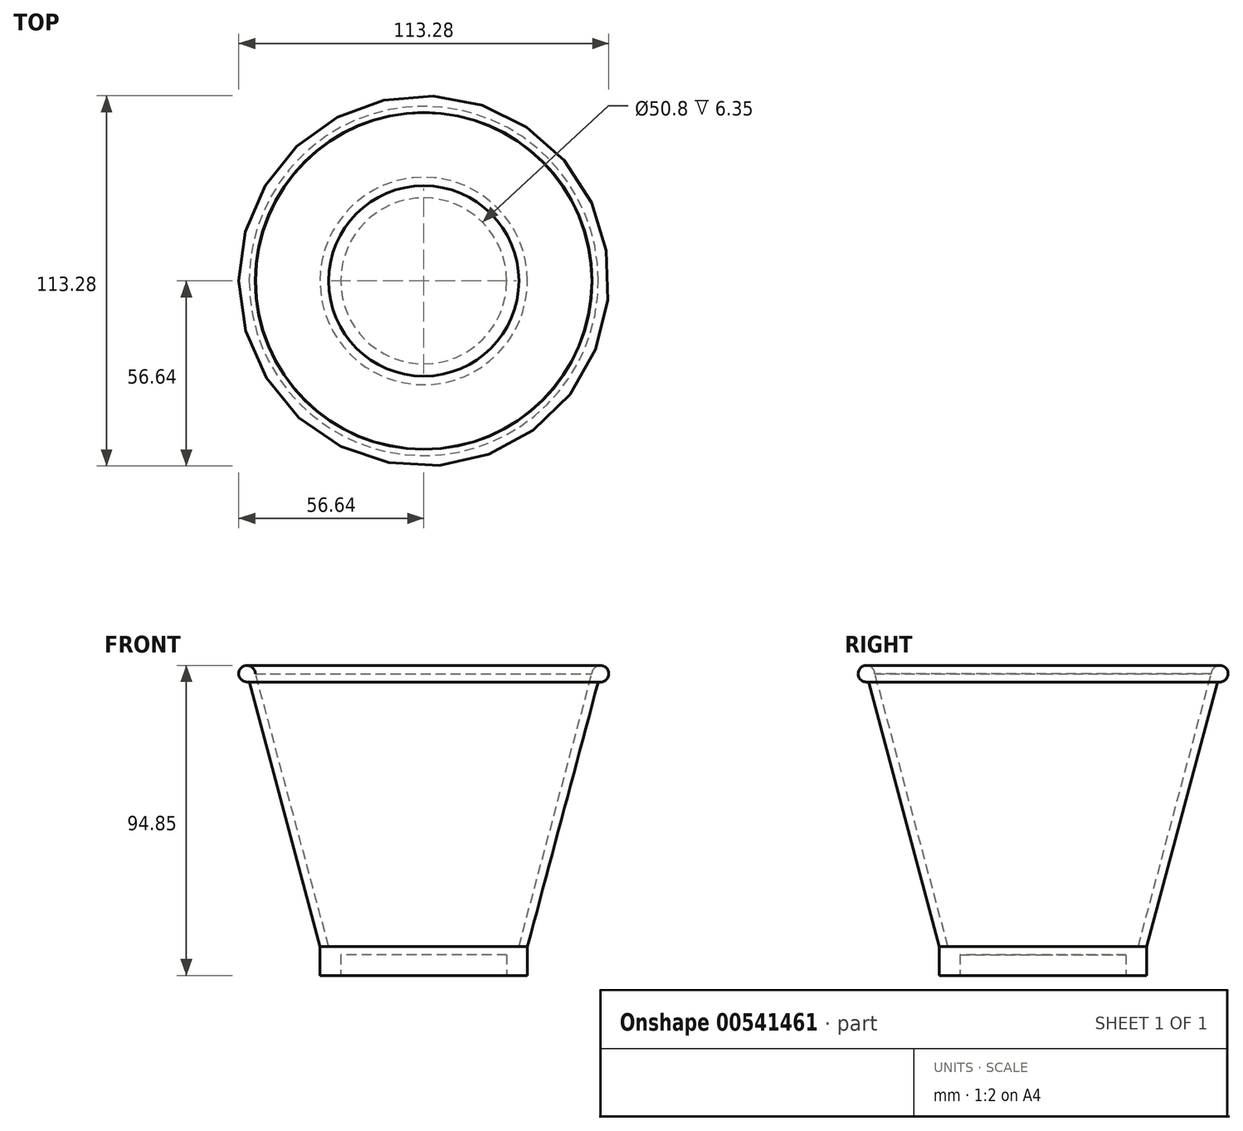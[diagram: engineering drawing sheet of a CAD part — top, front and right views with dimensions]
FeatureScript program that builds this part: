
annotation { "Feature Type Name" : "Feature", "Feature Type Description" : "" }
export const myFeature = defineFeature(function(context is Context, id is Id, definition is map)
    precondition{}
    {
        {
            var Q0;
            Q0=qCreatedBy(makeId("Top.planeOp"),FACE);
            var sketch = newSketch(context, id + "F0", { "sketchPlane" : qUnion([Q0])});
            skCircle(sketch, "E0", {"center": v(0, 0) * mm, "radius": 25.4 * mm});
            skCircle(sketch, "E1.0", {"center": v(0, 0) * mm, "radius": 31.75 * mm});
            skSolve(sketch);
        }
        {
            var Q0;
            Q0 = qSketchRegion(id + "F0", true);
            extrude(context, id + "F1", {"entities" : qUnion([Q0]), "depth" : 6.35 * mm, "offsetDistance" : 25.4 * mm});
        }
        {
            var Q0;
            Q0=makeQuery(id+"F1.opExtrude","CAP_FACE",FACE,{"disambiguationData":[OSD([sQuery(id+"F0.wireOp",EDGE,"E0"),sQuery(id+"F0.wireOp",EDGE,"E1.0")])],"isStart":false});
            var sketch = newSketch(context, id + "F2", { "sketchPlane" : qUnion([Q0])});
            skCircle(sketch, "E2", {"center": v(0, 0) * mm, "radius": 31.75 * mm});
            skSolve(sketch);
        }
        {
            var Q0;
            Q0 = qSketchRegion(id + "F2", true);
            extrude(context, id + "F3", {"entities" : qUnion([Q0]), "operationType" : NewBodyOperationType.ADD, "depth" : 2.54 * mm, "offsetDistance" : 25.4 * mm});
        }
        {
            var Q0;
            Q0=qCreatedBy(makeId("Front.planeOp"),FACE);
            var sketch = newSketch(context, id + "F4", { "sketchPlane" : qUnion([Q0])});
            skLineSegment(sketch, "E3.0", {"start": v(-31.75, 8.9) * mm, "end": v(31.75, 8.9) * mm, "construction": true});
            skLineSegment(sketch, "E4", {"start": v(-31.75, 8.89) * mm, "end": v(-53.44, 89.85) * mm});
            skLineSegment(sketch, "E5", {"start": v(-51.56, 92.3) * mm, "end": v(-51.47, 92.3) * mm});
            skLineSegment(sketch, "E6", {"start": v(-51.47, 92.3) * mm, "end": v(-29.12, 8.89) * mm});
            skLineSegment(sketch, "E7", {"start": v(-29.12, 8.89) * mm, "end": v(-31.75, 8.89) * mm});
            skArc(sketch, "E8", {"start": v(-51.56, 92.3) * mm, "mid": v(-56.12, 93.85) * mm, "end": v(-53.44, 89.85) * mm});
            skLineSegment(sketch, "E9", {"start": v(0, 8.9) * mm, "end": v(0, 98.7) * mm, "construction": true});
            skPoint(sketch, "E9.endSnap0", {"position": v(0, 8.9) * mm});
            skSolve(sketch);
        }
        {
            var Q0;
            Q0 = qSketchRegion(id + "F4", true);
            var Q1;
            Q1=sQuery(id+"F4.wireOp",EDGE,"E9");
            revolve(context, id + "F5", {"operationType" : NewBodyOperationType.ADD, "entities" : qUnion([Q0]), "axis" : qUnion([Q1]), "revolveType" : RevolveType.FULL});
        }
    });
